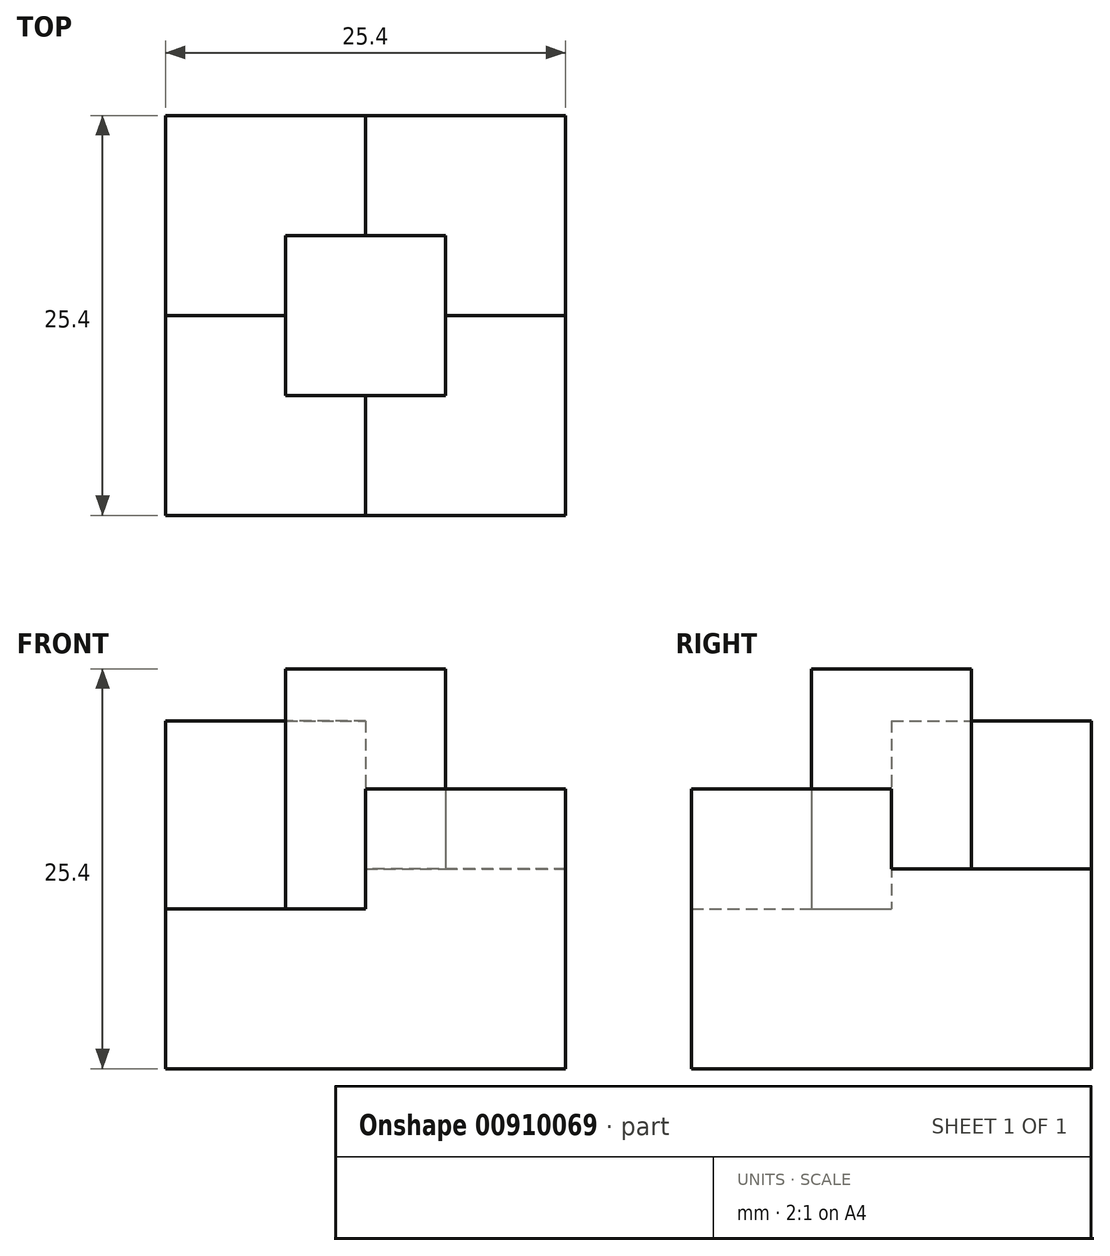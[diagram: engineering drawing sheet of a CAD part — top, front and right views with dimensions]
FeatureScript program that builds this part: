
annotation { "Feature Type Name" : "Feature", "Feature Type Description" : "" }
export const myFeature = defineFeature(function(context is Context, id is Id, definition is map)
    precondition{}
    {
        {
            var Q0;
            Q0=qCreatedBy(makeId("Top.planeOp"),FACE);
            var sketch = newSketch(context, id + "F0", { "sketchPlane" : qUnion([Q0])});
            skLineSegment(sketch, "E0.bottom", {"start": v(8.3, -9.68) * mm, "end": v(-17.1, -9.68) * mm});
            skLineSegment(sketch, "E0.top", {"start": v(8.3, 15.72) * mm, "end": v(-17.1, 15.72) * mm});
            skLineSegment(sketch, "E0.left", {"start": v(8.3, -9.68) * mm, "end": v(8.3, 15.72) * mm});
            skLineSegment(sketch, "E0.right", {"start": v(-17.1, -9.68) * mm, "end": v(-17.1, 15.72) * mm});
            skLineSegment(sketch, "E1.top", {"start": v(-9.49, 8.1) * mm, "end": v(0.67, 8.1) * mm});
            skLineSegment(sketch, "E1.left", {"start": v(-9.49, -2.06) * mm, "end": v(-9.49, 8.1) * mm});
            skLineSegment(sketch, "E1.right", {"start": v(0.67, -2.06) * mm, "end": v(0.67, 8.1) * mm});
            skLineSegment(sketch, "E2.left", {"start": v(-9.49, 3.02) * mm, "end": v(-9.62, 3.02) * mm});
            skLineSegment(sketch, "E2.right", {"start": v(0.67, 3.02) * mm, "end": v(0.54, 3.02) * mm});
            skLineSegment(sketch, "E3.bottom", {"start": v(-17.1, -9.68) * mm, "end": v(-4.4, -9.68) * mm});
            skLineSegment(sketch, "E3.left", {"start": v(-17.1, -9.68) * mm, "end": v(-17.1, -3.33) * mm});
            skLineSegment(sketch, "E3.right", {"start": v(-4.4, -9.68) * mm, "end": v(-4.4, -2) * mm});
            skLineSegment(sketch, "E4", {"start": v(-9.49, -2.06) * mm, "end": v(0.67, -2.06) * mm});
            skLineSegment(sketch, "E5", {"start": v(-4.4, 8.1) * mm, "end": v(-4.4, 15.72) * mm});
            skLineSegment(sketch, "E6", {"start": v(-9.49, 3.02) * mm, "end": v(-17.1, 3.02) * mm});
            skLineSegment(sketch, "E7", {"start": v(0.54, 3.02) * mm, "end": v(8.3, 3.02) * mm});
            skSolve(sketch);
        }
        {
            var Q0;
            {var subQ8=sQuery(id+"F0.wireOp",EDGE,"E2.left");Q0=makeQuery(id+"F0.imprint","IMPRINT",FACE,{"disambiguationData":[TD([[makeQuery(id+"F0.imprint","IMPRINT",EDGE,{"derivedFrom":subQ8}),-1.0]])]});}
            extrude(context, id + "F1", {"entities" : qUnion([Q0]), "depth" : 22.1 * mm, "offsetDistance" : 25.4 * mm});
        }
        {
            var Q0;
            {var subQ3=sQuery(id+"F0.wireOp",EDGE,"E5");Q0=makeQuery(id+"F0.imprint","IMPRINT",FACE,{"disambiguationData":[TD([[makeQuery(id+"F0.imprint","IMPRINT",EDGE,{"derivedFrom":subQ3}),-1.0]])]});}
            extrude(context, id + "F2", {"entities" : qUnion([Q0]), "operationType" : NewBodyOperationType.ADD, "depth" : 12.7 * mm, "offsetDistance" : 25.4 * mm});
        }
        {
            var Q0;
            {var subQ10=sQuery(id+"F0.wireOp",EDGE,"E2.left");Q0=makeQuery(id+"F0.imprint","IMPRINT",FACE,{"disambiguationData":[TD([[makeQuery(id+"F0.imprint","IMPRINT",EDGE,{"derivedFrom":subQ10}),1.0]])]});}
            extrude(context, id + "F3", {"entities" : qUnion([Q0]), "operationType" : NewBodyOperationType.ADD, "depth" : 10.16 * mm, "offsetDistance" : 25.4 * mm});
        }
        {
            var Q0;
            {var subQ7=sQuery(id+"F0.wireOp",EDGE,"E7");Q0=makeQuery(id+"F0.imprint","IMPRINT",FACE,{"disambiguationData":[TD([[makeQuery(id+"F0.imprint","IMPRINT",EDGE,{"derivedFrom":subQ7}),-1.0]])]});}
            extrude(context, id + "F4", {"entities" : qUnion([Q0]), "operationType" : NewBodyOperationType.ADD, "depth" : 17.78 * mm, "offsetDistance" : 25.4 * mm});
        }
        {
            var Q0;
            {var subQ0=sQuery(id+"F0.wireOp",EDGE,"E1.left");var subQ1=sQuery(id+"F0.wireOp",EDGE,"E1.top");var subQ2=makeQuery(id+"F0.imprint","INTERSECT",VERTEX,{"derivedFrom":[subQ1,subQ0]});Q0=makeQuery(id+"F0.imprint","IMPRINT",FACE,{"disambiguationData":[TD([[makeQuery(id+"F0.imprint","IMPRINT",EDGE,{"disambiguationData":[TD([[subQ2,-1.0]])],"derivedFrom":subQ1}),-1.0]])]});}
            extrude(context, id + "F5", {"entities" : qUnion([Q0]), "operationType" : NewBodyOperationType.ADD, "depth" : 25.4 * mm, "offsetDistance" : 25.4 * mm});
        }
    });
